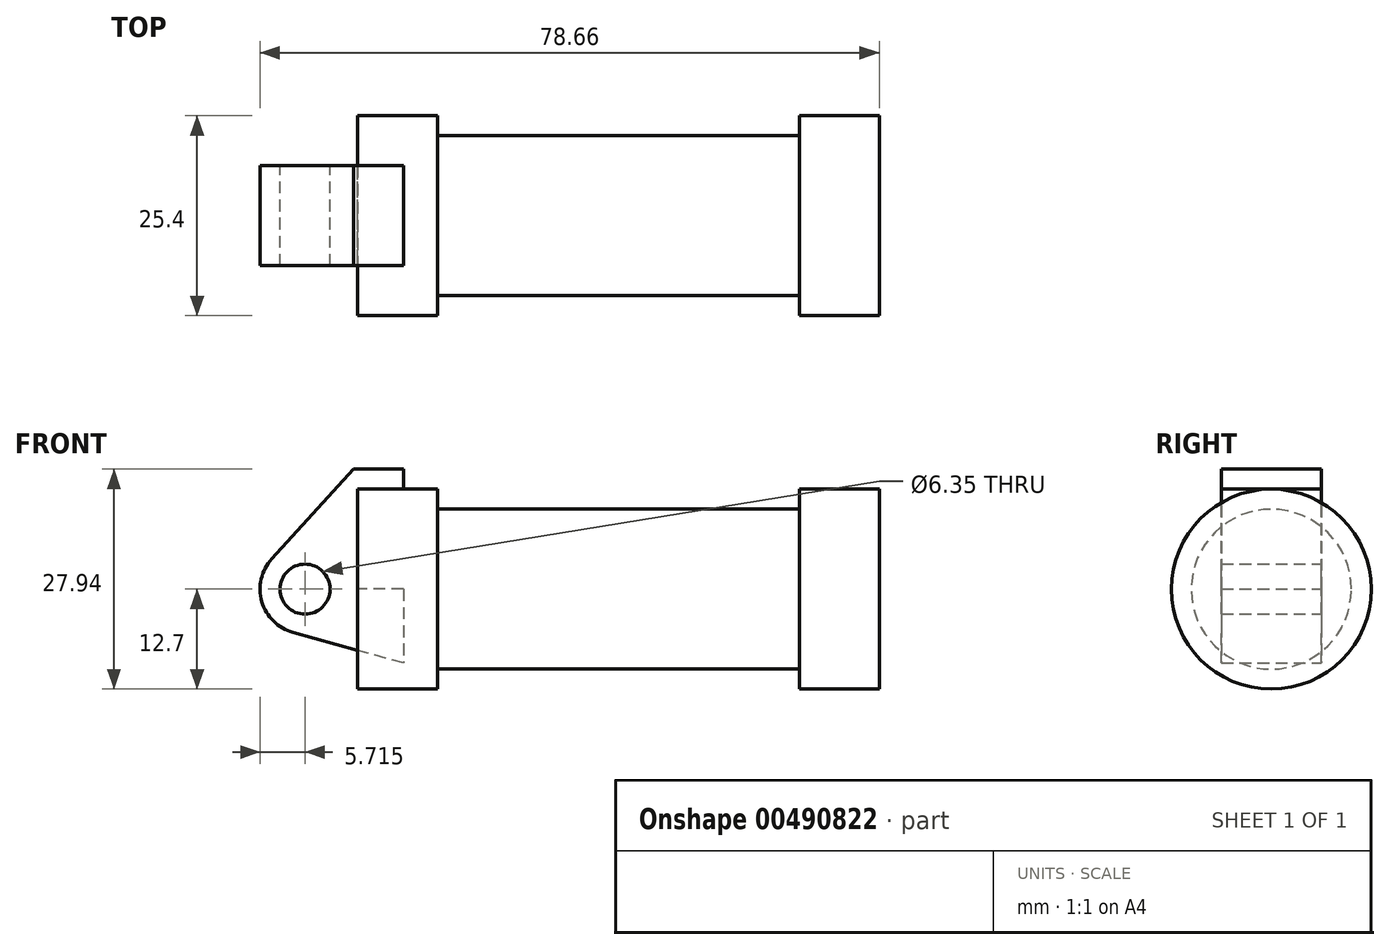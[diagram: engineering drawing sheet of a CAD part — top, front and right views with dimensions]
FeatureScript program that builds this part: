
annotation { "Feature Type Name" : "Feature", "Feature Type Description" : "" }
export const myFeature = defineFeature(function(context is Context, id is Id, definition is map)
    precondition{}
    {
        {
            var Q0;
            Q0=qCreatedBy(makeId("Front.planeOp"),FACE);
            var sketch = newSketch(context, id + "F0", { "sketchPlane" : qUnion([Q0])});
            skLineSegment(sketch, "E0", {"start": v(0, 0) * mm, "end": v(0, 12.7) * mm});
            skLineSegment(sketch, "E1", {"start": v(0, 12.7) * mm, "end": v(10.16, 12.7) * mm});
            skLineSegment(sketch, "E2", {"start": v(10.16, 12.7) * mm, "end": v(10.16, 10.16) * mm});
            skLineSegment(sketch, "E3", {"start": v(10.16, 10.16) * mm, "end": v(56.13, 10.16) * mm});
            skLineSegment(sketch, "E4", {"start": v(56.13, 10.16) * mm, "end": v(56.13, 12.7) * mm});
            skLineSegment(sketch, "E5", {"start": v(56.13, 12.7) * mm, "end": v(66.3, 12.7) * mm});
            skLineSegment(sketch, "E6", {"start": v(66.3, 12.7) * mm, "end": v(66.3, 0) * mm});
            skLineSegment(sketch, "E7", {"start": v(66.3, 0) * mm, "end": v(0, 0) * mm});
            skLineSegment(sketch, "E8", {"start": v(5.84, 15.24) * mm, "end": v(-0.5, 15.24) * mm});
            skLineSegment(sketch, "E9", {"start": v(-0.5, 15.24) * mm, "end": v(-10.88, 3.85) * mm});
            skLineSegment(sketch, "E10", {"start": v(0, 0) * mm, "end": v(-6.65, 0) * mm});
            skCircle(sketch, "E11", {"center": v(-6.65, 0) * mm, "radius": 5.72 * mm});
            skCircle(sketch, "E12", {"center": v(-6.65, 0) * mm, "radius": 3.18 * mm});
            skLineSegment(sketch, "E13", {"start": v(5.84, 15.24) * mm, "end": v(5.84, -9.4) * mm});
            skLineSegment(sketch, "E14", {"start": v(5.84, -9.4) * mm, "end": v(-8.18, -5.5) * mm});
            skSolve(sketch);
        }
        {
            var Q0;
            {var subQ0=sQuery(id+"F0.wireOp",EDGE,"E2");Q0=makeQuery(id+"F0.imprint","IMPRINT",FACE,{"disambiguationData":[TD([[makeQuery(id+"F0.imprint","IMPRINT",EDGE,{"derivedFrom":subQ0}),-1.0]])]});}
            var Q1;
            {var subQ0=sQuery(id+"F0.wireOp",EDGE,"E0");Q1=makeQuery(id+"F0.imprint","IMPRINT",FACE,{"disambiguationData":[TD([[makeQuery(id+"F0.imprint","IMPRINT",EDGE,{"derivedFrom":subQ0}),-1.0]])]});}
            var Q2;
            Q2=sQuery(id+"F0.wireOp",EDGE,"E7");
            revolve(context, id + "F1", {"entities" : qUnion([Q0, Q1]), "axis" : qUnion([Q2]), "revolveType" : RevolveType.FULL});
        }
        {
            var Q0;
            {var subQ1=sQuery(id+"F0.wireOp",EDGE,"E0");Q0=makeQuery(id+"F0.imprint","IMPRINT",FACE,{"disambiguationData":[TD([[makeQuery(id+"F0.imprint","IMPRINT",EDGE,{"derivedFrom":subQ1}),1.0]])]});}
            var Q1;
            {var subQ5=sQuery(id+"F0.wireOp",EDGE,"E12");Q1=makeQuery(id+"F0.imprint","IMPRINT",FACE,{"disambiguationData":[TD([[makeQuery(id+"F0.imprint","IMPRINT",EDGE,{"derivedFrom":subQ5}),-1.0]])]});}
            var Q2;
            {var subQ0=sQuery(id+"F0.wireOp",EDGE,"E14");Q2=makeQuery(id+"F0.imprint","IMPRINT",FACE,{"disambiguationData":[TD([[makeQuery(id+"F0.imprint","IMPRINT",EDGE,{"derivedFrom":subQ0}),-1.0]])]});}
            extrude(context, id + "F2", {"entities" : qUnion([Q0, Q1, Q2]), "depth" : 6.35 * mm, "hasSecondDirection" : true, "secondDirectionOppositeDirection" : true, "secondDirectionDepth" : 6.35 * mm});
        }
    });
